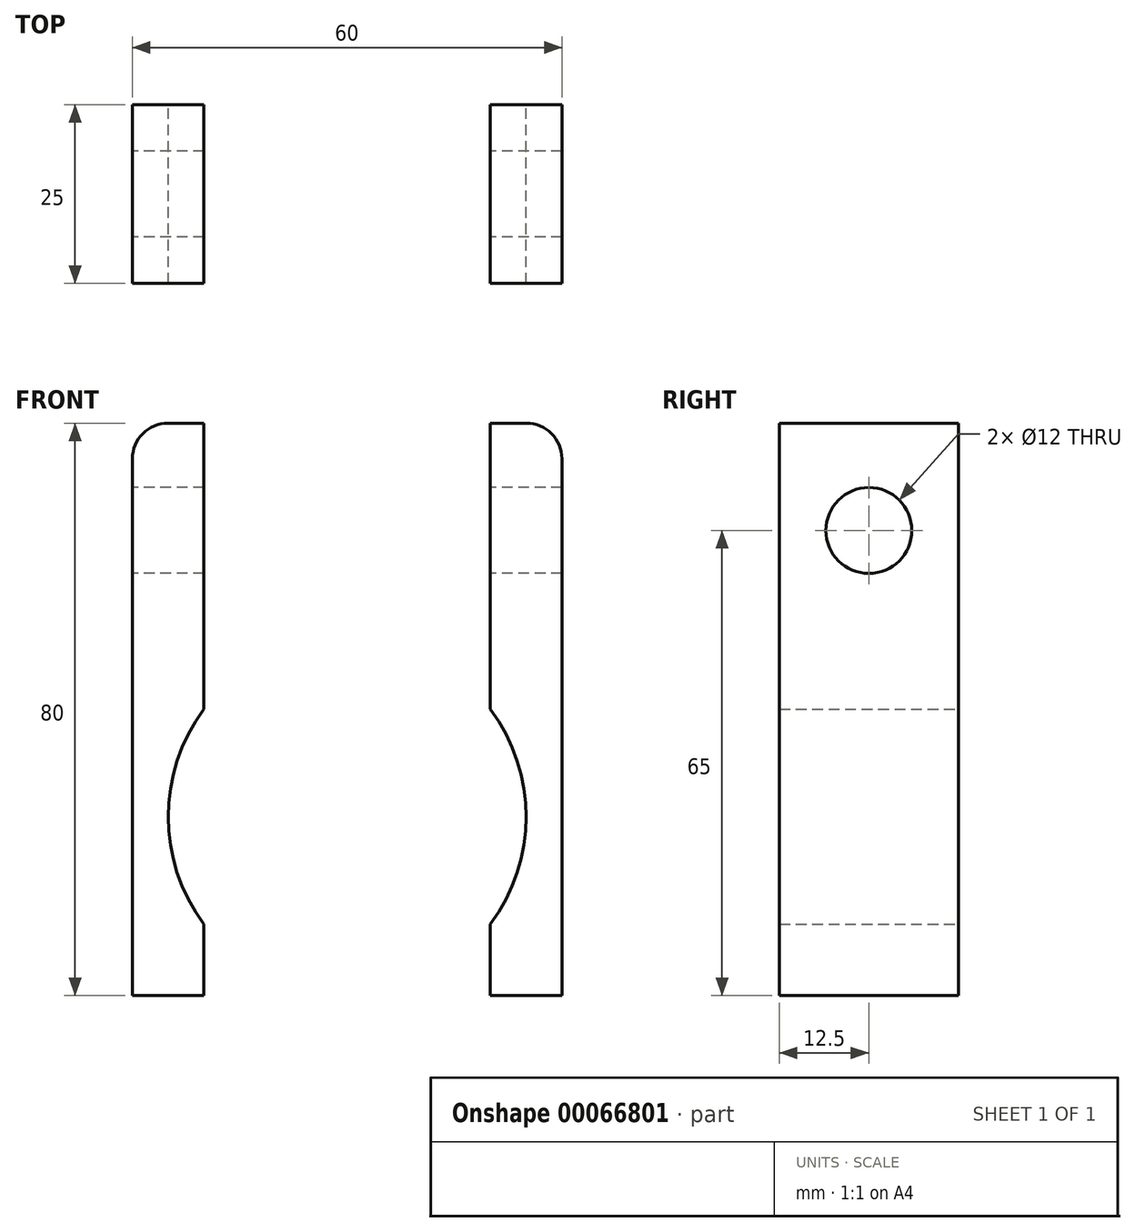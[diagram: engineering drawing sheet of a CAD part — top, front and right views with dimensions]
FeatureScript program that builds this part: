
annotation { "Feature Type Name" : "Feature", "Feature Type Description" : "" }
export const myFeature = defineFeature(function(context is Context, id is Id, definition is map)
    precondition{}
    {
        {
            var Q0;
            Q0=qCreatedBy(makeId("Front.planeOp"),FACE);
            var sketch = newSketch(context, id + "F0", { "sketchPlane" : qUnion([Q0])});
            skLineSegment(sketch, "E0.bottom", {"start": v(-30, -40) * mm, "end": v(-20, -40) * mm});
            skLineSegment(sketch, "E0.top", {"start": v(-30, 40) * mm, "end": v(-20, 40) * mm});
            skLineSegment(sketch, "E0.left", {"start": v(-30, -40) * mm, "end": v(-30, 40) * mm});
            skLineSegment(sketch, "E0.right", {"start": v(30, -40) * mm, "end": v(30, 40) * mm});
            skPoint(sketch, "E0.middle", {"position": v(0, 0) * mm});
            skLineSegment(sketch, "E1.left", {"start": v(20, -40) * mm, "end": v(20, -30) * mm});
            skLineSegment(sketch, "E1.right", {"start": v(-20, -40) * mm, "end": v(-20, -30) * mm});
            skLineSegment(sketch, "E2", {"start": v(0, -40) * mm, "end": v(0, -15) * mm});
            skPoint(sketch, "E2.endSnap0", {"position": v(0, -40) * mm});
            skArc(sketch, "E3", {"start": v(-20, 0) * mm, "mid": v(-25, -15) * mm, "end": v(-20, -30) * mm});
            skLineSegment(sketch, "E4.trimOffspring", {"start": v(-20, 0) * mm, "end": v(-20, 40) * mm});
            skLineSegment(sketch, "E5.trimOffspring", {"start": v(20, 0) * mm, "end": v(20, 40) * mm});
            skArc(sketch, "E6.trimOffspring", {"start": v(20, -30) * mm, "mid": v(25, -15) * mm, "end": v(20, 0) * mm});
            skLineSegment(sketch, "E7.trimOffspring", {"start": v(20, -40) * mm, "end": v(30, -40) * mm});
            skPoint(sketch, "E8.orphan", {"position": v(20, -50) * mm});
            skPoint(sketch, "E9.orphan", {"position": v(-20, -50) * mm});
            skPoint(sketch, "E10.orphan", {"position": v(-20, 50) * mm});
            skPoint(sketch, "E11.orphan", {"position": v(20, 50) * mm});
            skLineSegment(sketch, "E12.trimOffspring", {"start": v(20, 40) * mm, "end": v(30, 40) * mm});
            skSolve(sketch);
        }
        {
            var Q0;
            Q0=makeQuery(id+"F0.imprint","IMPRINT",FACE,{"disambiguationData":[TD([[makeQuery(id+"F0.imprint","IMPRINT",EDGE,{"derivedFrom":sQuery(id+"F0.wireOp",EDGE,"E0.bottom")}),1.0]])]});
            var Q1;
            Q1=makeQuery(id+"F0.imprint","IMPRINT",FACE,{"disambiguationData":[TD([[makeQuery(id+"F0.imprint","IMPRINT",EDGE,{"derivedFrom":sQuery(id+"F0.wireOp",EDGE,"E0.right")}),1.0]])]});
            extrude(context, id + "F1", {"entities" : qUnion([Q0, Q1]), "depth" : 25 * mm});
        }
        {
            var Q0;
            Q0=qCreatedBy(makeId("Right.planeOp"),FACE);
            var sketch = newSketch(context, id + "F2", { "sketchPlane" : qUnion([Q0])});
            skLineSegment(sketch, "E13", {"start": v(0, 0) * mm, "end": v(-12.5, 0) * mm});
            skLineSegment(sketch, "E14", {"start": v(-12.5, 0) * mm, "end": v(-12.5, 25) * mm});
            skCircle(sketch, "E15", {"center": v(-12.5, 25) * mm, "radius": 6 * mm});
            skSolve(sketch);
        }
        {
            var Q0;
            Q0=makeQuery(id+"F2.imprint","IMPRINT",FACE,{"disambiguationData":[TD([[makeQuery(id+"F2.imprint","IMPRINT",EDGE,{"derivedFrom":sQuery(id+"F2.wireOp",EDGE,"E15")}),1.0]])]});
            extrude(context, id + "F3", {"entities" : qUnion([Q0]), "operationType" : NewBodyOperationType.REMOVE, "depth" : 50 * mm, "hasSecondDirection" : true, "secondDirectionOppositeDirection" : true, "secondDirectionDepth" : 30 * mm});
        }
        {
            var Q0;
            Q0=makeQuery(id+"F2.imprint","IMPRINT",FACE,{"disambiguationData":[TD([[makeQuery(id+"F2.imprint","IMPRINT",EDGE,{"derivedFrom":sQuery(id+"F2.wireOp",EDGE,"E15")}),1.0]])]});
            extrude(context, id + "F4", {"entities" : qUnion([Q0]), "operationType" : NewBodyOperationType.REMOVE, "oppositeDirection" : true, "depth" : 30 * mm});
        }
        {
            var Q0;
            Q0=makeQuery(id+"F1.opExtrude","SWEPT_EDGE",EDGE,{"disambiguationData":[OSD([sQuery(id+"F0.wireOp",EDGE,"E0.right"),sQuery(id+"F0.wireOp",EDGE,"E12.trimOffspring")])]});
            var Q1;
            Q1=makeQuery(id+"F1.opExtrude","SWEPT_EDGE",EDGE,{"disambiguationData":[OSD([sQuery(id+"F0.wireOp",EDGE,"E0.top"),sQuery(id+"F0.wireOp",EDGE,"E0.left")])]});
            fillet(context, id + "F5", {"entities" : qUnion([Q0, Q1]), "radius" : 5 * mm, "allowEdgeOverflow" : false});
        }
    });
